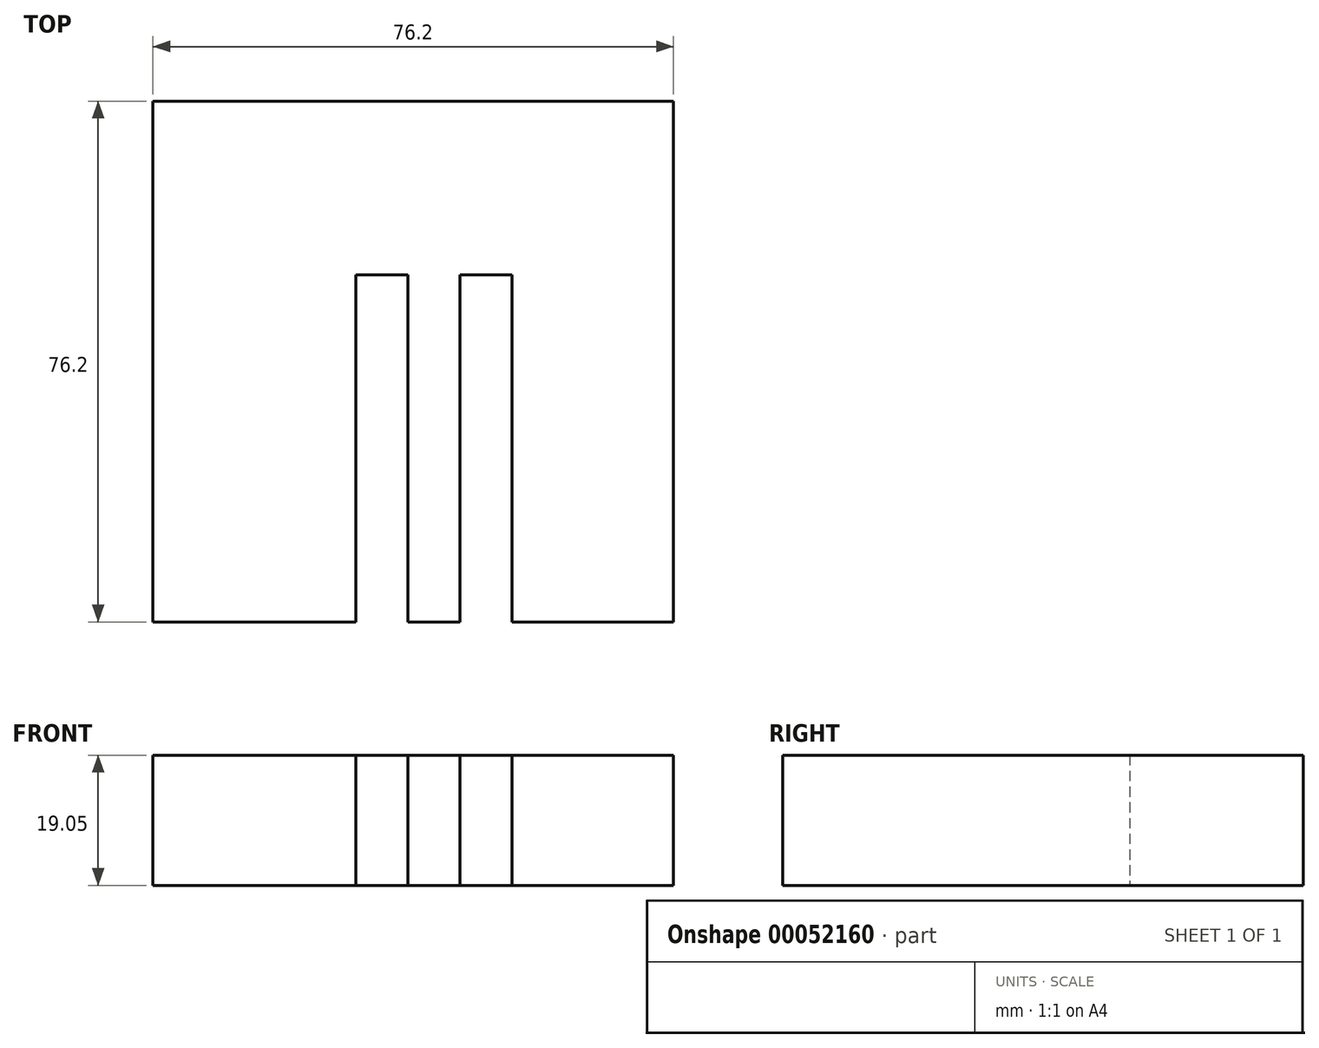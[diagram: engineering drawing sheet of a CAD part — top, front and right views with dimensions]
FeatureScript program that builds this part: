
annotation { "Feature Type Name" : "Feature", "Feature Type Description" : "" }
export const myFeature = defineFeature(function(context is Context, id is Id, definition is map)
    precondition{}
    {
        {
            var Q0;
            Q0=qCreatedBy(makeId("Top.planeOp"),FACE);
            var sketch = newSketch(context, id + "F0", { "sketchPlane" : qUnion([Q0])});
            skLineSegment(sketch, "E0.rect.bottom", {"start": v(38.1, 38.1) * mm, "end": v(-38.1, 38.1) * mm});
            skLineSegment(sketch, "E0.rect.top", {"start": v(38.1, -38.1) * mm, "end": v(14.49, -38.1) * mm});
            skLineSegment(sketch, "E0.rect.left", {"start": v(38.1, 38.1) * mm, "end": v(38.1, -38.1) * mm});
            skLineSegment(sketch, "E0.rect.right", {"start": v(-38.1, 38.1) * mm, "end": v(-38.1, -38.1) * mm});
            skPoint(sketch, "E0.rect.middle", {"position": v(0, 0) * mm});
            skLineSegment(sketch, "E1", {"start": v(-8.37, -38.1) * mm, "end": v(-8.37, 12.7) * mm});
            skLineSegment(sketch, "E2", {"start": v(-8.37, 12.7) * mm, "end": v(-0.75, 12.7) * mm});
            skLineSegment(sketch, "E3", {"start": v(-0.75, 12.7) * mm, "end": v(-0.75, -38.1) * mm});
            skLineSegment(sketch, "E4", {"start": v(6.87, -38.1) * mm, "end": v(6.87, 12.7) * mm});
            skLineSegment(sketch, "E5", {"start": v(6.87, 12.7) * mm, "end": v(14.49, 12.7) * mm});
            skLineSegment(sketch, "E6", {"start": v(14.49, 12.7) * mm, "end": v(14.49, -38.1) * mm});
            skLineSegment(sketch, "E7.trimOffspring", {"start": v(-8.37, -38.1) * mm, "end": v(-38.1, -38.1) * mm});
            skLineSegment(sketch, "E8.trimOffspring", {"start": v(6.87, -38.1) * mm, "end": v(-0.75, -38.1) * mm});
            skSolve(sketch);
        }
        {
            var Q0;
            Q0=makeQuery(id+"F0.imprint","IMPRINT",FACE,{"disambiguationData":[TD([[makeQuery(id+"F0.imprint","IMPRINT",EDGE,{"derivedFrom":sQuery(id+"F0.wireOp",EDGE,"E0.rect.bottom")}),1.0]])]});
            extrude(context, id + "F1", {"entities" : qUnion([Q0]), "depth" : 19.05 * mm});
        }
    });
